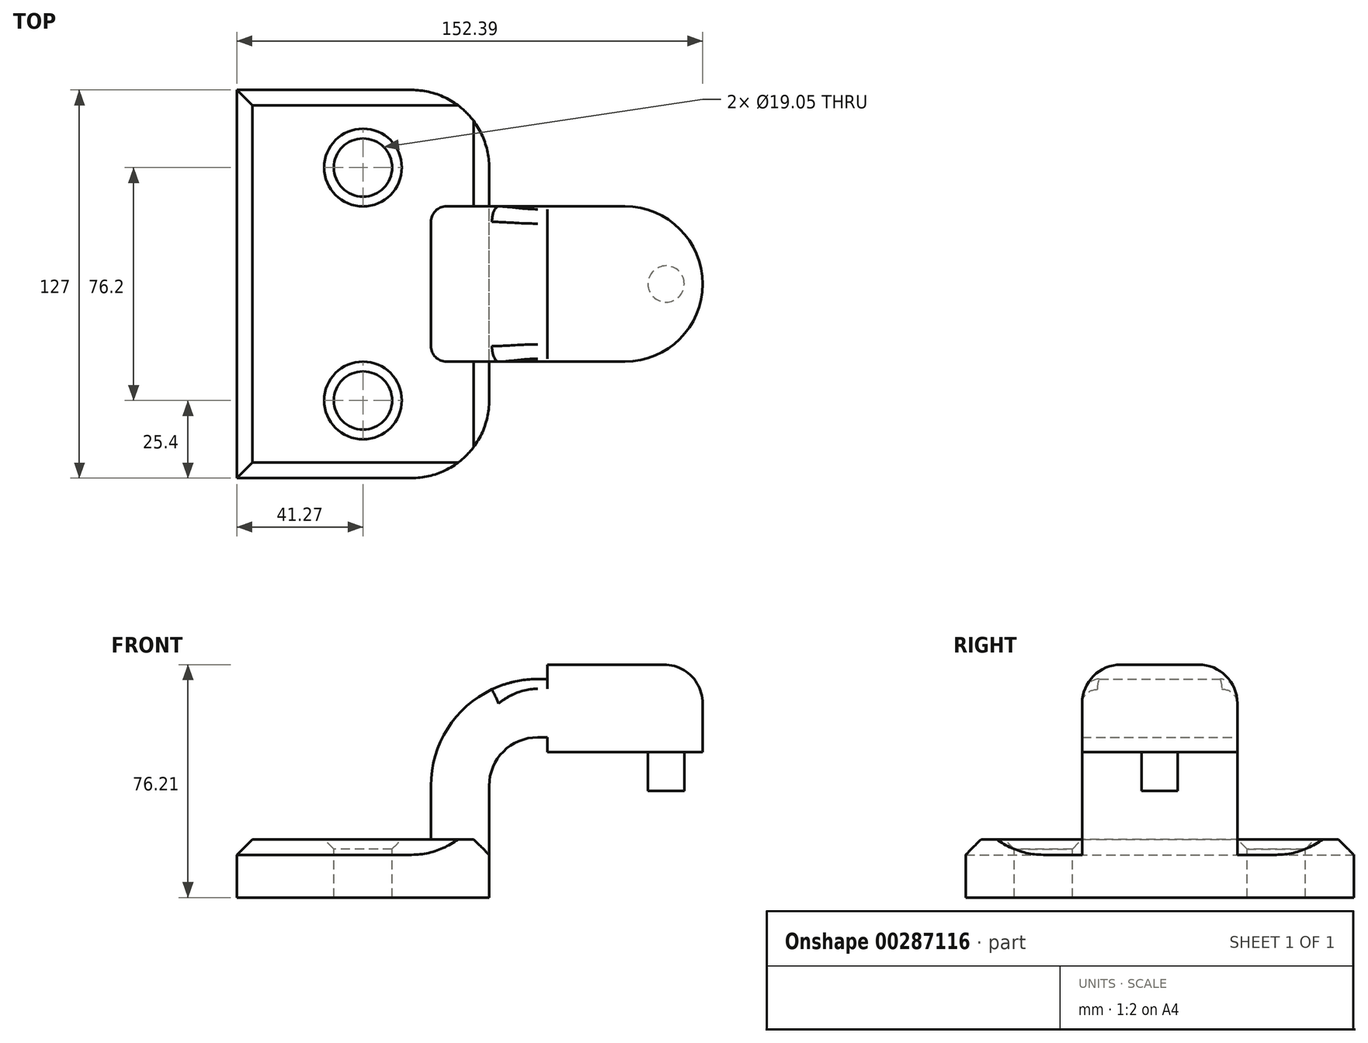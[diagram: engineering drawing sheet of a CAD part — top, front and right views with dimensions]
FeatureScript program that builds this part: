
annotation { "Feature Type Name" : "Feature", "Feature Type Description" : "" }
export const myFeature = defineFeature(function(context is Context, id is Id, definition is map)
    precondition{}
    {
        {
            var Q0;
            Q0=qCreatedBy(makeId("Front.planeOp"),FACE);
            var sketch = newSketch(context, id + "F0", { "sketchPlane" : qUnion([Q0])});
            skLineSegment(sketch, "E0.bottom", {"start": v(41.28, -9.52) * mm, "end": v(-41.28, -9.52) * mm});
            skLineSegment(sketch, "E0.top", {"start": v(41.27, 9.53) * mm, "end": v(-41.28, 9.53) * mm});
            skLineSegment(sketch, "E0.left", {"start": v(41.28, -9.52) * mm, "end": v(41.28, 9.53) * mm});
            skLineSegment(sketch, "E0.right", {"start": v(-41.28, -9.52) * mm, "end": v(-41.28, 9.53) * mm});
            skPoint(sketch, "E0.middle", {"position": v(0, 0) * mm});
            skLineSegment(sketch, "E1", {"start": v(41.27, 9.53) * mm, "end": v(41.27, 27) * mm});
            skLineSegment(sketch, "E2.bottom", {"start": v(111.12, 66.68) * mm, "end": v(60.32, 66.68) * mm});
            skLineSegment(sketch, "E2.top", {"start": v(111.12, 38.1) * mm, "end": v(60.32, 38.1) * mm});
            skLineSegment(sketch, "E2.left", {"start": v(111.12, 66.68) * mm, "end": v(111.12, 38.1) * mm});
            skLineSegment(sketch, "E2.right", {"start": v(60.32, 66.68) * mm, "end": v(60.32, 38.1) * mm});
            skPoint(sketch, "E2.middle", {"position": v(85.72, 52.39) * mm});
            skArc(sketch, "E3", {"start": v(41.27, 27) * mm, "mid": v(45.92, 38.23) * mm, "end": v(57.15, 42.88) * mm});
            skLineSegment(sketch, "E4", {"start": v(57.15, 42.88) * mm, "end": v(85.73, 42.88) * mm});
            skLineSegment(sketch, "E5.0", {"start": v(57.15, 61.93) * mm, "end": v(85.73, 61.93) * mm});
            skArc(sketch, "E5.1", {"start": v(22.23, 27) * mm, "mid": v(32.45, 51.7) * mm, "end": v(57.15, 61.93) * mm});
            skLineSegment(sketch, "E5.2", {"start": v(22.22, 9.53) * mm, "end": v(22.22, 27) * mm});
            skLineSegment(sketch, "E6", {"start": v(85.72, 38.1) * mm, "end": v(85.72, 66.68) * mm});
            skFitSpline(sketch, "E7", {"points": [v(-41.28, 9.53) * mm, v(57.15, 61.93) * mm], "startDerivative": vector(4.01, 120.96) * mm, "endDerivative": vector(164.81, -3.41) * mm});
            skSolve(sketch);
        }
        {
            var Q0;
            Q0=makeQuery(id+"F0.imprint","IMPRINT",FACE,{"disambiguationData":[TD([[makeQuery(id+"F0.imprint","IMPRINT",EDGE,{"derivedFrom":sQuery(id+"F0.wireOp",EDGE,"E0.bottom")}),-1.0]])]});
            extrude(context, id + "F1", {"entities" : qUnion([Q0]), "endBound" : BoundingType.SYMMETRIC, "depth" : 127 * mm});
        }
        {
            var Q0;
            {var subQ6=sQuery(id+"F0.wireOp",EDGE,"E1");Q0=makeQuery(id+"F0.imprint","IMPRINT",FACE,{"disambiguationData":[TD([[makeQuery(id+"F0.imprint","IMPRINT",EDGE,{"derivedFrom":subQ6}),1.0]])]});}
            var Q1;
            {var subQ0=sQuery(id+"F0.wireOp",EDGE,"E2.right");var subQ1=sQuery(id+"F0.wireOp",EDGE,"E2.bottom");var subQ2=makeQuery(id+"F0.imprint","INTERSECT",VERTEX,{"derivedFrom":[subQ1,subQ0]});Q1=makeQuery(id+"F0.imprint","IMPRINT",FACE,{"disambiguationData":[TD([[makeQuery(id+"F0.imprint","IMPRINT",EDGE,{"disambiguationData":[TD([[subQ2,1.0]])],"derivedFrom":subQ1}),1.0]])]});}
            var Q2;
            {var subQ0=sQuery(id+"F0.wireOp",EDGE,"E2.right");var subQ1=sQuery(id+"F0.wireOp",EDGE,"E2.top");var subQ2=makeQuery(id+"F0.imprint","INTERSECT",VERTEX,{"derivedFrom":[subQ1,subQ0]});Q2=makeQuery(id+"F0.imprint","IMPRINT",FACE,{"disambiguationData":[TD([[makeQuery(id+"F0.imprint","IMPRINT",EDGE,{"disambiguationData":[TD([[subQ2,1.0]])],"derivedFrom":subQ1}),-1.0]])]});}
            var Q3;
            {var subQ0=sQuery(id+"F0.wireOp",EDGE,"E5.0");var subQ1=sQuery(id+"F0.wireOp",EDGE,"E2.right");var subQ2=makeQuery(id+"F0.imprint","INTERSECT",VERTEX,{"derivedFrom":[subQ1,subQ0]});Q3=makeQuery(id+"F0.imprint","IMPRINT",FACE,{"disambiguationData":[TD([[makeQuery(id+"F0.imprint","IMPRINT",EDGE,{"disambiguationData":[TD([[subQ2,-1.0]])],"derivedFrom":subQ1}),1.0]])]});}
            extrude(context, id + "F2", {"entities" : qUnion([Q0, Q1, Q2, Q3]), "operationType" : NewBodyOperationType.ADD, "endBound" : BoundingType.SYMMETRIC, "depth" : 50.8 * mm});
        }
        {
            var Q0;
            {var subQ0=sQuery(id+"F0.wireOp",EDGE,"E2.left");Q0=makeQuery(id+"F0.imprint","IMPRINT",FACE,{"disambiguationData":[TD([[makeQuery(id+"F0.imprint","IMPRINT",EDGE,{"derivedFrom":subQ0}),-1.0]])]});}
            var Q1;
            Q1=sQuery(id+"F0.wireOp",EDGE,"E6");
            revolve(context, id + "F3", {"operationType" : NewBodyOperationType.ADD, "entities" : qUnion([Q0]), "axis" : qUnion([Q1]), "revolveType" : RevolveType.FULL});
        }
        {
            var Q0;
            Q0=makeQuery(id+"F0.imprint","IMPRINT",FACE,{"disambiguationData":[TD([[makeQuery(id+"F0.imprint","IMPRINT",EDGE,{"derivedFrom":sQuery(id+"F0.wireOp",EDGE,"E5.1")}),1.0]])]});
            extrude(context, id + "F4", {"entities" : qUnion([Q0]), "operationType" : NewBodyOperationType.ADD, "endBound" : BoundingType.SYMMETRIC, "depth" : 6.35 * mm});
        }
        {
            var Q0;
            Q0=makeQuery(id+"F3.opRevolve","SWEPT_EDGE",EDGE,{"disambiguationData":[OSD([sQuery(id+"F0.wireOp",EDGE,"E2.bottom"),sQuery(id+"F0.wireOp",EDGE,"E2.left")])]});
            fillet(context, id + "F5", {"entities" : qUnion([Q0]), "radius" : 12.7 * mm, "tangentPropagation" : true, "allowEdgeOverflow" : false});
        }
        {
            var Q0;
            {var subQ0=sQuery(id+"F0.wireOp",EDGE,"E2.top");Q0=makeQuery(id+"F3.boolean.opBoolean","MERGE",FACE,{"derivedFrom":[makeQuery(id+"F2.opExtrude","SWEPT_FACE",FACE,{"disambiguationData":[OSD([subQ0])]}),makeQuery(id+"F3.opRevolve","SWEPT_FACE",FACE,{"disambiguationData":[OSD([subQ0])]})]});}
            var sketch = newSketch(context, id + "F6", { "sketchPlane" : qUnion([Q0])});
            skCircle(sketch, "E8", {"center": v(99.18, 0) * mm, "radius": 5.94 * mm});
            skSolve(sketch);
        }
        {
            var Q0;
            Q0=makeQuery(id+"F6.imprint","IMPRINT",FACE,{"disambiguationData":[TD([[makeQuery(id+"F6.imprint","IMPRINT",EDGE,{"derivedFrom":sQuery(id+"F6.wireOp",EDGE,"E8")}),1.0]])]});
            extrude(context, id + "F7", {"entities" : qUnion([Q0]), "operationType" : NewBodyOperationType.ADD, "depth" : 12.7 * mm});
        }
        {
            var Q0;
            {var subQ3=sQuery(id+"F0.wireOp",EDGE,"E0.top");var subQ4=sQuery(id+"F0.wireOp",EDGE,"E0.right");var subQ5=sQuery(id+"F0.wireOp",EDGE,"E0.left");Q0=makeQuery(id+"F4.boolean.opBoolean","SPLIT",FACE,{"disambiguationData":[TD([makeQuery(id+"F1.opExtrude","CAP_FACE",FACE,{"disambiguationData":[OSD([sQuery(id+"F0.wireOp",EDGE,"E0.bottom"),subQ3,subQ5,subQ4])],"isStart":true})])],"derivedFrom":makeQuery(id+"F1.opExtrude","SWEPT_FACE",FACE,{"disambiguationData":[OSD([subQ3])]})});}
            var sketch = newSketch(context, id + "F8", { "sketchPlane" : qUnion([Q0])});
            skPoint(sketch, "E9", {"position": v(0, 38.1) * mm});
            skPoint(sketch, "E10", {"position": v(0, -38.1) * mm});
            skSolve(sketch);
        }
        {
            var Q0;
            Q0=sQuery(id+"F8.wireOp",VERTEX,"E9");
            var Q1;
            Q1=sQuery(id+"F8.wireOp",VERTEX,"E10");
            var Q2;
            Q2=makeQuery(id+"F1.opExtrude","SWEPT_BODY",BODY,{"disambiguationData":[OSD([sQuery(id+"F0.wireOp",EDGE,"E0.bottom"),sQuery(id+"F0.wireOp",EDGE,"E0.top"),sQuery(id+"F0.wireOp",EDGE,"E0.left"),sQuery(id+"F0.wireOp",EDGE,"E0.right")])]});
            hole(context, id + "F9", {"style" : HoleStyle.C_SINK, "endStyle" : HoleEndStyle.THROUGH, "holeDiameter" : 19.05 * mm, "cSinkDiameter" : 25.4 * mm, "cSinkAngle" : 90 * degree, "tappedDepth" : 12.7 * mm, "tapClearance" : 3, "locations" : qUnion([Q0, Q1]), "scope" : qUnion([Q2])});
        }
        {
            var Q0;
            Q0=makeQuery(id+"F1.opExtrude","CAP_EDGE",EDGE,{"disambiguationData":[OSD([sQuery(id+"F0.wireOp",EDGE,"E0.top")])],"isStart":false});
            var Q1;
            Q1=makeQuery(id+"F1.opExtrude","CAP_EDGE",EDGE,{"disambiguationData":[OSD([sQuery(id+"F0.wireOp",EDGE,"E0.top")])],"isStart":true});
            var Q2;
            {var subQ0=sQuery(id+"F0.wireOp",EDGE,"E1");var subQ1=sQuery(id+"F0.wireOp",EDGE,"E0.top");var subQ2=sQuery(id+"F0.wireOp",EDGE,"E0.left");Q2=makeQuery(id+"F2.boolean.opBoolean","SPLIT",EDGE,{"disambiguationData":[TD([makeQuery(id+"F1.opExtrude","CAP_FACE",FACE,{"disambiguationData":[OSD([sQuery(id+"F0.wireOp",EDGE,"E0.bottom"),subQ1,subQ2,sQuery(id+"F0.wireOp",EDGE,"E0.right")])],"isStart":true})])],"derivedFrom":makeQuery(id+"F1.opExtrude","SWEPT_EDGE",EDGE,{"disambiguationData":[OSD([subQ1,subQ2,subQ0])]})});}
            var Q3;
            {var subQ0=sQuery(id+"F0.wireOp",EDGE,"E0.left");var subQ1=sQuery(id+"F0.wireOp",EDGE,"E1");var subQ2=sQuery(id+"F0.wireOp",EDGE,"E0.top");Q3=makeQuery(id+"F2.boolean.opBoolean","SPLIT",EDGE,{"disambiguationData":[TD([makeQuery(id+"F1.opExtrude","CAP_FACE",FACE,{"disambiguationData":[OSD([sQuery(id+"F0.wireOp",EDGE,"E0.bottom"),subQ2,subQ0,sQuery(id+"F0.wireOp",EDGE,"E0.right")])],"isStart":false})])],"derivedFrom":makeQuery(id+"F1.opExtrude","SWEPT_EDGE",EDGE,{"disambiguationData":[OSD([subQ2,subQ0,subQ1])]})});}
            var Q4;
            {var subQ0=sQuery(id+"F0.wireOp",EDGE,"E0.right");var subQ1=sQuery(id+"F0.wireOp",EDGE,"E0.top");var subQ2=sQuery(id+"F0.wireOp",EDGE,"E7");Q4=makeQuery(id+"F4.boolean.opBoolean","SPLIT",EDGE,{"disambiguationData":[TD([makeQuery(id+"F1.opExtrude","CAP_FACE",FACE,{"disambiguationData":[OSD([sQuery(id+"F0.wireOp",EDGE,"E0.bottom"),subQ1,sQuery(id+"F0.wireOp",EDGE,"E0.left"),subQ0])],"isStart":false})])],"derivedFrom":makeQuery(id+"F1.opExtrude","SWEPT_EDGE",EDGE,{"disambiguationData":[OSD([subQ1,subQ0,subQ2])]})});}
            var Q5;
            {var subQ0=sQuery(id+"F0.wireOp",EDGE,"E0.right");var subQ1=sQuery(id+"F0.wireOp",EDGE,"E0.top");var subQ2=sQuery(id+"F0.wireOp",EDGE,"E7");Q5=makeQuery(id+"F4.boolean.opBoolean","SPLIT",EDGE,{"disambiguationData":[TD([makeQuery(id+"F1.opExtrude","CAP_FACE",FACE,{"disambiguationData":[OSD([sQuery(id+"F0.wireOp",EDGE,"E0.bottom"),subQ1,sQuery(id+"F0.wireOp",EDGE,"E0.left"),subQ0])],"isStart":true})])],"derivedFrom":makeQuery(id+"F1.opExtrude","SWEPT_EDGE",EDGE,{"disambiguationData":[OSD([subQ1,subQ0,subQ2])]})});}
            chamfer(context, id + "F10", {"entities" : qUnion([Q0, Q1, Q2, Q3, Q4, Q5]), "width" : 5.08 * mm, "tangentPropagation" : true});
        }
        {
            var Q0;
            Q0=makeQuery(id+"F1.opExtrude","CAP_EDGE",EDGE,{"disambiguationData":[OSD([sQuery(id+"F0.wireOp",EDGE,"E0.left")])],"isStart":false});
            var Q1;
            Q1=makeQuery(id+"F1.opExtrude","CAP_EDGE",EDGE,{"disambiguationData":[OSD([sQuery(id+"F0.wireOp",EDGE,"E0.left")])],"isStart":true});
            fillet(context, id + "F11", {"entities" : qUnion([Q0, Q1]), "radius" : 25.4 * mm, "tangentPropagation" : true, "allowEdgeOverflow" : false});
        }
        {
            var Q0;
            {var subQ0=sQuery(id+"F0.wireOp",EDGE,"E7");var subQ1=sQuery(id+"F0.wireOp",EDGE,"E5.2");var subQ2=sQuery(id+"F0.wireOp",EDGE,"E5.1");var subQ3=sQuery(id+"F0.wireOp",EDGE,"E0.top");var subQ5=sQuery(id+"F0.wireOp",EDGE,"E2.bottom");Q0=makeQuery(id+"F5.opFillet","BLEND_EDGE",EDGE,{"blendedFrom":[makeQuery(id+"F2.opExtrude","CAP_EDGE",EDGE,{"disambiguationData":[OSD([subQ5])],"isStart":false}),makeQuery(id+"F4.boolean.opBoolean","SPLIT",FACE,{"disambiguationData":[TD([makeQuery(id+"F4.opExtrude","CAP_FACE",FACE,{"disambiguationData":[OSD([subQ3,subQ2,subQ1,subQ0])],"isStart":false})])],"derivedFrom":makeQuery(id+"F2.opExtrude","SWEPT_FACE",FACE,{"disambiguationData":[OSD([subQ2])]})})],"blendedInto":[makeQuery(id+"F4.boolean.opBoolean","SPLIT",FACE,{"disambiguationData":[TD([makeQuery(id+"F4.opExtrude","CAP_FACE",FACE,{"disambiguationData":[OSD([subQ3,subQ2,subQ1,subQ0])],"isStart":false})])],"derivedFrom":makeQuery(id+"F2.opExtrude","SWEPT_FACE",FACE,{"disambiguationData":[OSD([subQ2])]})})]});}
            var Q1;
            {var subQ0=sQuery(id+"F0.wireOp",EDGE,"E5.2");var subQ1=sQuery(id+"F0.wireOp",EDGE,"E5.1");var subQ3=sQuery(id+"F0.wireOp",EDGE,"E2.bottom");var subQ4=sQuery(id+"F0.wireOp",EDGE,"E0.top");var subQ5=sQuery(id+"F0.wireOp",EDGE,"E7");Q1=makeQuery(id+"F5.opFillet","BLEND_EDGE",EDGE,{"blendedFrom":[makeQuery(id+"F2.opExtrude","CAP_EDGE",EDGE,{"disambiguationData":[OSD([subQ3])],"isStart":true}),makeQuery(id+"F4.boolean.opBoolean","SPLIT",FACE,{"disambiguationData":[TD([makeQuery(id+"F4.opExtrude","CAP_FACE",FACE,{"disambiguationData":[OSD([subQ4,subQ1,subQ0,subQ5])],"isStart":true})])],"derivedFrom":makeQuery(id+"F2.opExtrude","SWEPT_FACE",FACE,{"disambiguationData":[OSD([subQ1])]})})],"blendedInto":[makeQuery(id+"F4.boolean.opBoolean","SPLIT",FACE,{"disambiguationData":[TD([makeQuery(id+"F4.opExtrude","CAP_FACE",FACE,{"disambiguationData":[OSD([subQ4,subQ1,subQ0,subQ5])],"isStart":true})])],"derivedFrom":makeQuery(id+"F2.opExtrude","SWEPT_FACE",FACE,{"disambiguationData":[OSD([subQ1])]})})]});}
            var Q2;
            Q2=makeQuery(id+"F4.opExtrude","CAP_EDGE",EDGE,{"disambiguationData":[OSD([sQuery(id+"F0.wireOp",EDGE,"E7")])],"isStart":true});
            fillet(context, id + "F12", {"entities" : qUnion([Q0, Q1, Q2]), "radius" : 5.08 * mm, "tangentPropagation" : true, "allowEdgeOverflow" : false});
        }
    });
